# Revit family: Univers-IP44-syst-Unterputz-NoHosted-AT-de
name_source: partatom
category: Electrical Equipment
units: mm (PartAtom-declared; Revit-internal decimal feet)

## family parameters
Always vertical = Yes
Cut with Voids When Loaded = No
Panel Configuration = Two Columns, Circuits Across
Part Type = Panelboard
Room Calculation Point = No
Round Connector Dimension = Use Diameter
Shared = No
Work Plane-Based = Yes

## types (56) — shared parameters
Default Elevation = 1219 mm
EF000003 - Montageart = EV001247 - Aufputz/Unterputz
EF000007 - Farbe = EV000202 - weiß
EF000049 - Tiefe = 161 mm  [stored 0.528215 ft]
EF000218 - Einbautiefe = 161 mm  [stored 0.528215 ft]
EF000339 - Art der Abdeckung = EV004216 - Tür
EF001062 - EMV-Ausführung = No
EF001088 - Anbaumöglichkeit = Yes
EF001596 - Werkstoff des Gehäuses = EV000179 - Stahl
EF002950 - Breite in Teilungseinheiten = 12
EF004462 - Art der Schließung = EV000154 - sonstige
EF005474 - Schutzart (IP) = EV006418 - IP44
EF006244 - Transparenter Deckel/Tür = No
EF006306 - Mit Schloss = No
EF015776 - Erdungsklemmenblock = No
EF015777 - Neutralleiterklemmenblock = No
EF015941 - Signaldurchlassende Tür = No
HG000002 - Mit tür = Yes
HG000003 - Bereich = Univers
HG000005 - Dicke = 3 mm  [stored 0.00984252 ft]
HG000006 - Unterputz = Yes
HG000011 - Leere Reihen von unten = No
Manufacturer = Hager
Type Comments = Univers
zero-valued in all types: HG000007 - Anzahl der leeren Spalten

## per-type parameters (varying)
| type | EF000008 - Breite | EF000040 - Höhe | EF000116 - RAL-Nummer | EF000118 - Mit Montageplatte | EF000266 - Anzahl der Reihen | EF000332 - Einbauhöhe | EF000846 - Einbaubreite | EF001131 - Innentiefe | EF001134 - DIN-Schiene | EF009212 - Ausführung Deckel | HG000001 - Anzahl der Spalten | HG000004 - Herstellerreferenz | HG000008 - Anzahl der leeren Reihen | HG000009 - Doppelflügeligen Tür | HG000010 - Asymmetrische Türen | Model |
| Unterputz IP44 B1050 H1100 T161 12 Teilungseinheiten - FWB74N | 1050 mm | 1100 mm | 0 | No | 20 | 1100 mm | 1050 mm | 161 mm  [stored 0.528215 ft] | Yes | EV009916 - mit Ausschnitt | 4 | FWB74N | 8 | Yes | No | FWB74N |
| Unterputz IP44 B1050 H1100 T161 12 Teilungseinheiten - FWB74S | 1050 mm | 1100 mm | 9010 | No | 28 | 1100 mm | 1050 mm | 161 mm  [stored 0.528215 ft] | Yes | EV009916 - mit Ausschnitt | 4 | FWB74S | 0 | Yes | No | FWB74S |
| Unterputz IP44 B1050 H1100 T161 12 Teilungseinheiten - FWQ74N | 1050 mm | 1100 mm | 0 | Yes | 20 | 1100 mm | 1050 mm | 161 mm  [stored 0.528215 ft] | No | EV009916 - mit Ausschnitt | 4 | FWQ74N | 8 | Yes | No | FWQ74N |
| Unterputz IP44 B1050 H1100 T161 12 Teilungseinheiten - FWQ74P | 1050 mm | 1100 mm | 0 | Yes | 28 | 1100 mm | 1050 mm | 161 mm  [stored 0.528215 ft] | No | EV009916 - mit Ausschnitt | 4 | FWQ74P | 0 | Yes | No | FWQ74P |
| Unterputz IP44 B1050 H500 T161 12 Teilungseinheiten - FWB34S | 1050 mm | 500 mm  [stored 1.64042 ft] | 9010 | No | 12 | 500 mm  [stored 1.64042 ft] | 1050 mm | 161 mm  [stored 0.528215 ft] | Yes | EV009916 - mit Ausschnitt | 4 | FWB34S | 0 | Yes | No | FWB34S |
| Unterputz IP44 B1050 H500 T161 12 Teilungseinheiten - FWQ34P | 1050 mm | 500 mm  [stored 1.64042 ft] | 0 | Yes | 12 | 500 mm  [stored 1.64042 ft] | 1050 mm | 161 mm  [stored 0.528215 ft] | No | EV009916 - mit Ausschnitt | 4 | FWQ34P | 0 | Yes | No | FWQ34P |
| Unterputz IP44 B1050 H650 T161 12 Teilungseinheiten - FWB44S | 1050 mm | 650 mm  [stored 2.13255 ft] | 9010 | No | 16 | 650 mm  [stored 2.13255 ft] | 1050 mm | 161 mm  [stored 0.528215 ft] | Yes | EV009916 - mit Ausschnitt | 4 | FWB44S | 0 | Yes | No | FWB44S |
| Unterputz IP44 B1050 H650 T161 12 Teilungseinheiten - FWQ44P | 1050 mm | 650 mm  [stored 2.13255 ft] | 0 | Yes | 16 | 650 mm  [stored 2.13255 ft] | 1050 mm | 161 mm  [stored 0.528215 ft] | No | EV009916 - mit Ausschnitt | 4 | FWQ44P | 0 | Yes | No | FWQ44P |
| Unterputz IP44 B1050 H800 T161 12 Teilungseinheiten - FWB54S | 1050 mm | 800 mm  [stored 2.62467 ft] | 9010 | No | 20 | 800 mm  [stored 2.62467 ft] | 1050 mm | 161 mm  [stored 0.528215 ft] | Yes | EV009916 - mit Ausschnitt | 4 | FWB54S | 0 | Yes | No | FWB54S |
| Unterputz IP44 B1050 H800 T161 12 Teilungseinheiten - FWQ54P | 1050 mm | 800 mm  [stored 2.62467 ft] | 0 | Yes | 20 | 800 mm  [stored 2.62467 ft] | 1050 mm | 161 mm  [stored 0.528215 ft] | No | EV009916 - mit Ausschnitt | 4 | FWQ54P | 0 | Yes | No | FWQ54P |
| Unterputz IP44 B1050 H950 T161 12 Teilungseinheiten - FWB64N | 1050 mm | 950 mm  [stored 3.1168 ft] | 0 | No | 16 | 950 mm  [stored 3.1168 ft] | 1050 mm | 161 mm  [stored 0.528215 ft] | Yes | EV009916 - mit Ausschnitt | 4 | FWB64N | 8 | Yes | No | FWB64N |
| Unterputz IP44 B1050 H950 T161 12 Teilungseinheiten - FWB64S | 1050 mm | 950 mm  [stored 3.1168 ft] | 9010 | No | 24 | 950 mm  [stored 3.1168 ft] | 1050 mm | 161 mm  [stored 0.528215 ft] | Yes | EV009916 - mit Ausschnitt | 4 | FWB64S | 0 | Yes | No | FWB64S |
| Unterputz IP44 B1050 H950 T161 12 Teilungseinheiten - FWQ64N | 1050 mm | 950 mm  [stored 3.1168 ft] | 0 | Yes | 16 | 950 mm  [stored 3.1168 ft] | 1050 mm | 161 mm  [stored 0.528215 ft] | No | EV009916 - mit Ausschnitt | 4 | FWQ64N | 8 | Yes | No | FWQ64N |
| Unterputz IP44 B1050 H950 T161 12 Teilungseinheiten - FWQ64P | 1050 mm | 950 mm  [stored 3.1168 ft] | 0 | Yes | 24 | 950 mm  [stored 3.1168 ft] | 1050 mm | 161 mm  [stored 0.528215 ft] | No | EV009916 - mit Ausschnitt | 4 | FWQ64P | 0 | Yes | No | FWQ64P |
| Unterputz IP44 B300 H1100 T161 12 Teilungseinheiten - FWB71S | 300 mm | 1100 mm | 9010 | No | 7 | 1100 mm | 300 mm | 161 mm  [stored 0.528215 ft] | Yes | EV009916 - mit Ausschnitt | 1 | FWB71S | 0 | No | No | FWB71S |
| Unterputz IP44 B300 H1100 T161 12 Teilungseinheiten - FWQ71P | 300 mm | 1100 mm | 0 | Yes | 7 | 1100 mm | 300 mm | 161 mm  [stored 0.528215 ft] | No | EV009916 - mit Ausschnitt | 1 | FWQ71P | 0 | No | No | FWQ71P |
| Unterputz IP44 B300 H500 T161 12 Teilungseinheiten - FWB31S | 300 mm | 500 mm  [stored 1.64042 ft] | 9010 | No | 3 | 500 mm  [stored 1.64042 ft] | 300 mm | 161 mm  [stored 0.528215 ft] | Yes | EV009916 - mit Ausschnitt | 1 | FWB31S | 0 | No | No | FWB31S |
| Unterputz IP44 B300 H500 T161 12 Teilungseinheiten - FWQ31P | 300 mm | 500 mm  [stored 1.64042 ft] | 0 | Yes | 3 | 500 mm  [stored 1.64042 ft] | 300 mm | 161 mm  [stored 0.528215 ft] | No | EV009916 - mit Ausschnitt | 1 | FWQ31P | 0 | No | No | FWQ31P |
| Unterputz IP44 B300 H650 T161 12 Teilungseinheiten - FWB41S | 300 mm | 650 mm  [stored 2.13255 ft] | 9010 | No | 4 | 650 mm  [stored 2.13255 ft] | 300 mm | 160 mm  [stored 0.524934 ft] | Yes | EV009916 - mit Ausschnitt | 1 | FWB41S | 0 | No | No | FWB41S |
| Unterputz IP44 B300 H650 T161 12 Teilungseinheiten - FWQ41P | 300 mm | 650 mm  [stored 2.13255 ft] | 0 | Yes | 4 | 650 mm  [stored 2.13255 ft] | 300 mm | 161 mm  [stored 0.528215 ft] | No | EV009916 - mit Ausschnitt | 1 | FWQ41P | 0 | No | No | FWQ41P |
| Unterputz IP44 B300 H800 T161 12 Teilungseinheiten - FWB51S | 300 mm | 800 mm  [stored 2.62467 ft] | 9010 | No | 5 | 800 mm  [stored 2.62467 ft] | 300 mm | 161 mm  [stored 0.528215 ft] | Yes | EV009916 - mit Ausschnitt | 1 | FWB51S | 0 | No | No | FWB51S |
| Unterputz IP44 B300 H800 T161 12 Teilungseinheiten - FWQ51P | 300 mm | 800 mm  [stored 2.62467 ft] | 0 | Yes | 5 | 800 mm  [stored 2.62467 ft] | 300 mm | 161 mm  [stored 0.528215 ft] | No | EV009916 - mit Ausschnitt | 1 | FWQ51P | 0 | No | No | FWQ51P |
| Unterputz IP44 B300 H950 T161 12 Teilungseinheiten - FWB61S | 300 mm | 950 mm  [stored 3.1168 ft] | 9010 | No | 6 | 950 mm  [stored 3.1168 ft] | 300 mm | 161 mm  [stored 0.528215 ft] | Yes | EV009916 - mit Ausschnitt | 1 | FWB61S | 0 | No | No | FWB61S |
| Unterputz IP44 B300 H950 T161 12 Teilungseinheiten - FWQ61P | 300 mm | 950 mm  [stored 3.1168 ft] | 0 | Yes | 6 | 950 mm  [stored 3.1168 ft] | 300 mm | 161 mm  [stored 0.528215 ft] | No | EV009916 - mit Ausschnitt | 1 | FWQ61P | 0 | No | No | FWQ61P |
| Unterputz IP44 B550 H1100 T161 12 Teilungseinheiten - FWB72N | 550 mm | 1100 mm | 0 | No | 10 | 1100 mm | 550 mm | 161 mm  [stored 0.528215 ft] | Yes | EV009916 - mit Ausschnitt | 2 | FWB72N | 4 | No | No | FWB72N |
| Unterputz IP44 B550 H1100 T161 12 Teilungseinheiten - FWB72S | 550 mm | 1100 mm | 9010 | No | 14 | 1100 mm | 550 mm | 161 mm  [stored 0.528215 ft] | Yes | EV009916 - mit Ausschnitt | 2 | FWB72S | 0 | No | No | FWB72S |
| Unterputz IP44 B550 H1100 T161 12 Teilungseinheiten - FWQ72N | 550 mm | 1100 mm | 0 | Yes | 10 | 1100 mm | 550 mm | 161 mm  [stored 0.528215 ft] | No | EV009916 - mit Ausschnitt | 2 | FWQ72N | 4 | No | No | FWQ72N |
| Unterputz IP44 B550 H1100 T161 12 Teilungseinheiten - FWQ72P | 550 mm | 1100 mm | 0 | Yes | 14 | 1100 mm | 550 mm | 161 mm  [stored 0.528215 ft] | No | EV009916 - mit Ausschnitt | 2 | FWQ72P | 0 | No | No | FWQ72P |
| Unterputz IP44 B550 H500 T161 12 Teilungseinheiten - FWB32S | 550 mm | 500 mm  [stored 1.64042 ft] | 9010 | No | 6 | 500 mm  [stored 1.64042 ft] | 550 mm | 161 mm  [stored 0.528215 ft] | Yes | EV009916 - mit Ausschnitt | 2 | FWB32S | 0 | No | No | FWB32S |
| Unterputz IP44 B550 H500 T161 12 Teilungseinheiten - FWQ32P | 550 mm | 500 mm  [stored 1.64042 ft] | 0 | Yes | 6 | 500 mm  [stored 1.64042 ft] | 550 mm | 161 mm  [stored 0.528215 ft] | No | EV009916 - mit Ausschnitt | 2 | FWQ32P | 0 | No | No | FWQ32P |
| Unterputz IP44 B550 H650 T161 12 Teilungseinheiten - FWB42S | 550 mm | 650 mm  [stored 2.13255 ft] | 9010 | No | 8 | 650 mm  [stored 2.13255 ft] | 550 mm | 161 mm  [stored 0.528215 ft] | Yes | EV009916 - mit Ausschnitt | 2 | FWB42S | 0 | No | No | FWB42S |
| Unterputz IP44 B550 H650 T161 12 Teilungseinheiten - FWQ42P | 550 mm | 650 mm  [stored 2.13255 ft] | 0 | Yes | 8 | 650 mm  [stored 2.13255 ft] | 550 mm | 161 mm  [stored 0.528215 ft] | No | EV009916 - mit Ausschnitt | 2 | FWQ42P | 0 | No | No | FWQ42P |
| Unterputz IP44 B550 H800 T161 12 Teilungseinheiten - FWB52N | 550 mm | 800 mm  [stored 2.62467 ft] | 0 | No | 6 | 800 mm  [stored 2.62467 ft] | 550 mm | 161 mm  [stored 0.528215 ft] | Yes | EV009916 - mit Ausschnitt | 2 | FWB52N | 4 | No | No | FWB52N |
| Unterputz IP44 B550 H800 T161 12 Teilungseinheiten - FWB52S | 550 mm | 800 mm  [stored 2.62467 ft] | 9010 | No | 10 | 800 mm  [stored 2.62467 ft] | 550 mm | 161 mm  [stored 0.528215 ft] | Yes | 0 | 2 | FWB52S | 0 | No | No | FWB52S |
| Unterputz IP44 B550 H800 T161 12 Teilungseinheiten - FWQ52N | 550 mm | 800 mm  [stored 2.62467 ft] | 0 | Yes | 6 | 800 mm  [stored 2.62467 ft] | 550 mm | 161 mm  [stored 0.528215 ft] | No | EV009916 - mit Ausschnitt | 2 | FWQ52N | 4 | No | No | FWQ52N |
| Unterputz IP44 B550 H800 T161 12 Teilungseinheiten - FWQ52P | 550 mm | 800 mm  [stored 2.62467 ft] | 0 | Yes | 10 | 800 mm  [stored 2.62467 ft] | 550 mm | 161 mm  [stored 0.528215 ft] | No | EV009916 - mit Ausschnitt | 2 | FWQ52P | 0 | No | No | FWQ52P |
| Unterputz IP44 B550 H950 T161 12 Teilungseinheiten - FWB62N | 550 mm | 950 mm  [stored 3.1168 ft] | 0 | No | 8 | 950 mm  [stored 3.1168 ft] | 550 mm | 161 mm  [stored 0.528215 ft] | Yes | EV009916 - mit Ausschnitt | 2 | FWB62N | 4 | No | No | FWB62N |
| Unterputz IP44 B550 H950 T161 12 Teilungseinheiten - FWB62S | 550 mm | 950 mm  [stored 3.1168 ft] | 9010 | No | 12 | 950 mm  [stored 3.1168 ft] | 550 mm | 160 mm  [stored 0.524934 ft] | Yes | EV009916 - mit Ausschnitt | 2 | FWB62S | 0 | No | No | FWB62S |
| Unterputz IP44 B550 H950 T161 12 Teilungseinheiten - FWQ62N | 550 mm | 950 mm  [stored 3.1168 ft] | 0 | Yes | 8 | 950 mm  [stored 3.1168 ft] | 550 mm | 161 mm  [stored 0.528215 ft] | No | EV009916 - mit Ausschnitt | 2 | FWQ62N | 4 | No | No | FWQ62N |
| Unterputz IP44 B550 H950 T161 12 Teilungseinheiten - FWQ62P | 550 mm | 950 mm  [stored 3.1168 ft] | 0 | Yes | 12 | 950 mm  [stored 3.1168 ft] | 550 mm | 161 mm  [stored 0.528215 ft] | No | EV009916 - mit Ausschnitt | 2 | FWQ62P | 0 | No | No | FWQ62P |
| Unterputz IP44 B800 H1100 T161 12 Teilungseinheiten - FWB73N | 800 mm  [stored 2.62467 ft] | 1100 mm | 0 | No | 15 | 1100 mm | 800 mm  [stored 2.62467 ft] | 161 mm  [stored 0.528215 ft] | Yes | EV009916 - mit Ausschnitt | 3 | FWB73N | 6 | Yes | Yes | FWB73N |
| Unterputz IP44 B800 H1100 T161 12 Teilungseinheiten - FWB73S | 800 mm  [stored 2.62467 ft] | 1100 mm | 9010 | No | 21 | 1100 mm | 800 mm  [stored 2.62467 ft] | 161 mm  [stored 0.528215 ft] | Yes | EV009916 - mit Ausschnitt | 3 | FWB73S | 0 | Yes | Yes | FWB73S |
| Unterputz IP44 B800 H1100 T161 12 Teilungseinheiten - FWQ73N | 800 mm  [stored 2.62467 ft] | 1100 mm | 0 | Yes | 15 | 1100 mm | 800 mm  [stored 2.62467 ft] | 161 mm  [stored 0.528215 ft] | No | EV009916 - mit Ausschnitt | 3 | FWQ73N | 6 | Yes | Yes | FWQ73N |
| Unterputz IP44 B800 H1100 T161 12 Teilungseinheiten - FWQ73P | 800 mm  [stored 2.62467 ft] | 1100 mm | 0 | Yes | 21 | 1100 mm | 800 mm  [stored 2.62467 ft] | 161 mm  [stored 0.528215 ft] | No | EV009916 - mit Ausschnitt | 3 | FWQ73P | 0 | Yes | Yes | FWQ73P |
| Unterputz IP44 B800 H500 T161 12 Teilungseinheiten - FWB33S | 800 mm  [stored 2.62467 ft] | 500 mm  [stored 1.64042 ft] | 9010 | No | 9 | 500 mm  [stored 1.64042 ft] | 800 mm  [stored 2.62467 ft] | 161 mm  [stored 0.528215 ft] | Yes | EV009916 - mit Ausschnitt | 3 | FWB33S | 0 | Yes | Yes | FWB33S |
| Unterputz IP44 B800 H500 T161 12 Teilungseinheiten - FWQ33P | 800 mm  [stored 2.62467 ft] | 500 mm  [stored 1.64042 ft] | 0 | Yes | 9 | 500 mm  [stored 1.64042 ft] | 800 mm  [stored 2.62467 ft] | 161 mm  [stored 0.528215 ft] | No | EV009916 - mit Ausschnitt | 3 | FWQ33P | 0 | Yes | Yes | FWQ33P |
| Unterputz IP44 B800 H650 T161 12 Teilungseinheiten - FWB43S | 800 mm  [stored 2.62467 ft] | 650 mm  [stored 2.13255 ft] | 9010 | No | 12 | 650 mm  [stored 2.13255 ft] | 800 mm  [stored 2.62467 ft] | 160 mm  [stored 0.524934 ft] | Yes | EV009916 - mit Ausschnitt | 3 | FWB43S | 0 | Yes | Yes | FWB43S |
| Unterputz IP44 B800 H650 T161 12 Teilungseinheiten - FWQ43P | 800 mm  [stored 2.62467 ft] | 650 mm  [stored 2.13255 ft] | 0 | Yes | 12 | 650 mm  [stored 2.13255 ft] | 800 mm  [stored 2.62467 ft] | 161 mm  [stored 0.528215 ft] | No | EV009916 - mit Ausschnitt | 3 | FWQ43P | 0 | Yes | Yes | FWQ43P |
| Unterputz IP44 B800 H800 T161 12 Teilungseinheiten - FWB53N | 800 mm  [stored 2.62467 ft] | 800 mm  [stored 2.62467 ft] | 0 | No | 9 | 800 mm  [stored 2.62467 ft] | 800 mm  [stored 2.62467 ft] | 161 mm  [stored 0.528215 ft] | Yes | EV009916 - mit Ausschnitt | 3 | FWB53N | 6 | Yes | Yes | FWB53N |
| Unterputz IP44 B800 H800 T161 12 Teilungseinheiten - FWB53S | 800 mm  [stored 2.62467 ft] | 800 mm  [stored 2.62467 ft] | 9010 | No | 15 | 800 mm  [stored 2.62467 ft] | 800 mm  [stored 2.62467 ft] | 160 mm  [stored 0.524934 ft] | Yes | EV009916 - mit Ausschnitt | 3 | FWB53S | 0 | Yes | Yes | FWB53S |
| Unterputz IP44 B800 H800 T161 12 Teilungseinheiten - FWQ53N | 800 mm  [stored 2.62467 ft] | 800 mm  [stored 2.62467 ft] | 0 | Yes | 9 | 800 mm  [stored 2.62467 ft] | 800 mm  [stored 2.62467 ft] | 161 mm  [stored 0.528215 ft] | No | EV009916 - mit Ausschnitt | 3 | FWQ53N | 6 | Yes | Yes | FWQ53N |
| Unterputz IP44 B800 H800 T161 12 Teilungseinheiten - FWQ53P | 800 mm  [stored 2.62467 ft] | 800 mm  [stored 2.62467 ft] | 0 | Yes | 15 | 800 mm  [stored 2.62467 ft] | 800 mm  [stored 2.62467 ft] | 161 mm  [stored 0.528215 ft] | No | EV009916 - mit Ausschnitt | 3 | FWQ53P | 0 | Yes | Yes | FWQ53P |
| Unterputz IP44 B800 H950 T161 12 Teilungseinheiten - FWB63N | 800 mm  [stored 2.62467 ft] | 950 mm  [stored 3.1168 ft] | 0 | No | 12 | 950 mm  [stored 3.1168 ft] | 800 mm  [stored 2.62467 ft] | 161 mm  [stored 0.528215 ft] | Yes | EV009916 - mit Ausschnitt | 3 | FWB63N | 6 | Yes | Yes | FWB63N |
| Unterputz IP44 B800 H950 T161 12 Teilungseinheiten - FWB63S | 800 mm  [stored 2.62467 ft] | 950 mm  [stored 3.1168 ft] | 9010 | No | 18 | 950 mm  [stored 3.1168 ft] | 800 mm  [stored 2.62467 ft] | 160 mm  [stored 0.524934 ft] | Yes | EV009916 - mit Ausschnitt | 3 | FWB63S | 0 | Yes | Yes | FWB63S |
| Unterputz IP44 B800 H950 T161 12 Teilungseinheiten - FWQ63N | 800 mm  [stored 2.62467 ft] | 950 mm  [stored 3.1168 ft] | 0 | Yes | 12 | 950 mm  [stored 3.1168 ft] | 800 mm  [stored 2.62467 ft] | 161 mm  [stored 0.528215 ft] | No | EV009916 - mit Ausschnitt | 3 | FWQ63N | 6 | Yes | Yes | FWQ63N |
| Unterputz IP44 B800 H950 T161 12 Teilungseinheiten - FWQ63P | 800 mm  [stored 2.62467 ft] | 950 mm  [stored 3.1168 ft] | 0 | Yes | 18 | 950 mm  [stored 3.1168 ft] | 800 mm  [stored 2.62467 ft] | 161 mm  [stored 0.528215 ft] | No | EV009916 - mit Ausschnitt | 3 | FWQ63P | 0 | Yes | Yes | FWQ63P |

note: [stored X ft] marks values corroborated as IEEE doubles in the binary element streams (Revit-internal decimal feet)

## geometry (parser evidence)
native form markers: Sweep x14
no freeform markers — native parametric forms only
